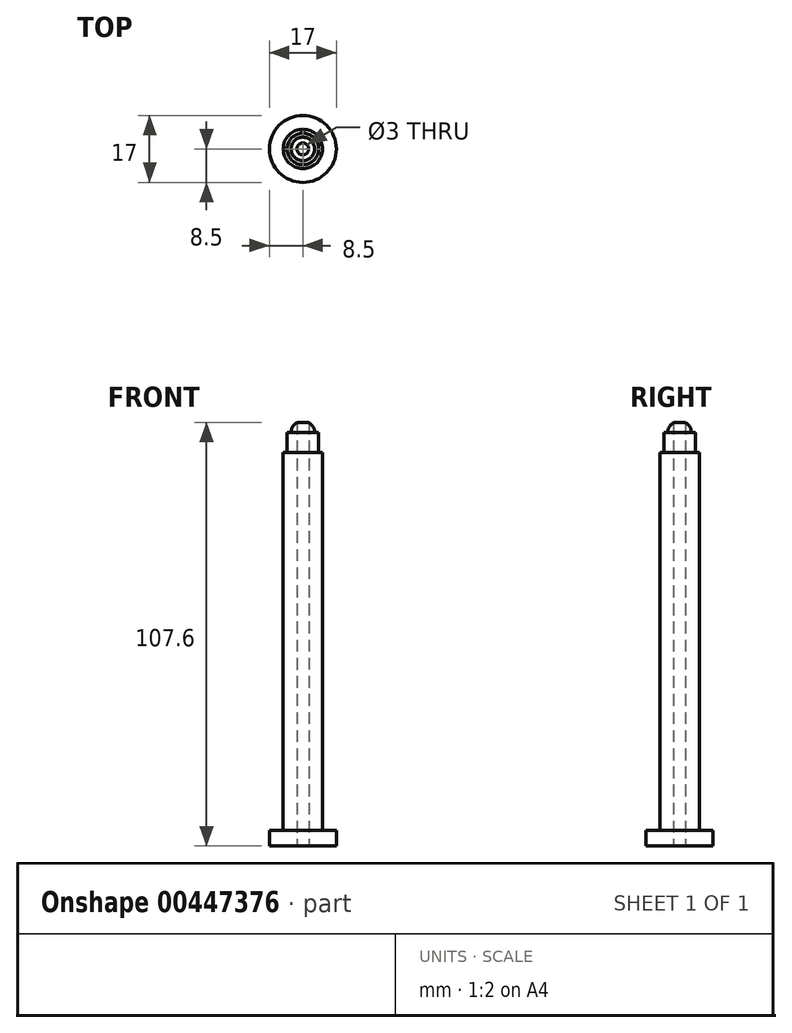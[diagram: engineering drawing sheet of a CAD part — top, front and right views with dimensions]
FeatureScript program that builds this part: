
annotation { "Feature Type Name" : "Feature", "Feature Type Description" : "" }
export const myFeature = defineFeature(function(context is Context, id is Id, definition is map)
    precondition{}
    {
        {
            var Q0;
            Q0=qCreatedBy(makeId("Top.planeOp"),FACE);
            var sketch = newSketch(context, id + "F0", { "sketchPlane" : qUnion([Q0])});
            skCircle(sketch, "E0", {"center": v(0, 0) * mm, "radius": 8.5 * mm});
            skSolve(sketch);
        }
        {
            var Q0;
            Q0=qSketchRegion(id+"F0",true);
            extrude(context, id + "F1", {"entities" : qUnion([Q0]), "depth" : 4 * mm});
        }
        {
            var Q0;
            Q0=qCreatedBy(makeId("Top.planeOp"),FACE);
            var sketch = newSketch(context, id + "F2", { "sketchPlane" : qUnion([Q0])});
            skCircle(sketch, "E1", {"center": v(0, 0) * mm, "radius": 5 * mm});
            skSolve(sketch);
        }
        {
            var Q0;
            Q0=qSketchRegion(id+"F2",true);
            extrude(context, id + "F3", {"entities" : qUnion([Q0]), "operationType" : NewBodyOperationType.ADD, "depth" : 100 * mm});
        }
        {
            var Q0;
            Q0=qCreatedBy(makeId("Right.planeOp"),FACE);
            var sketch = newSketch(context, id + "F4", { "sketchPlane" : qUnion([Q0])});
            skLineSegment(sketch, "E2", {"start": v(0, 105) * mm, "end": v(0, 100) * mm});
            skLineSegment(sketch, "E3", {"start": v(0, 100) * mm, "end": v(4, 100) * mm});
            skLineSegment(sketch, "E4", {"start": v(4, 100) * mm, "end": v(4, 105) * mm});
            skLineSegment(sketch, "E5", {"start": v(4, 105) * mm, "end": v(0, 105) * mm});
            skSolve(sketch);
        }
        {
            var Q0;
            Q0=makeQuery(id+"F4.imprint","IMPRINT",FACE,{"disambiguationData":[TD([[makeQuery(id+"F4.imprint","IMPRINT",EDGE,{"derivedFrom":sQuery(id+"F4.wireOp",EDGE,"E2")}),1.0]])]});
            var Q1;
            Q1=sQuery(id+"F4.wireOp",EDGE,"E2");
            revolve(context, id + "F5", {"operationType" : NewBodyOperationType.ADD, "entities" : qUnion([Q0]), "axis" : qUnion([Q1]), "revolveType" : RevolveType.FULL});
        }
        {
            var Q0;
            Q0=qCreatedBy(makeId("Right.planeOp"),FACE);
            var sketch = newSketch(context, id + "F6", { "sketchPlane" : qUnion([Q0])});
            skLineSegment(sketch, "E6", {"start": v(0, 108) * mm, "end": v(0, 105) * mm});
            skLineSegment(sketch, "E7", {"start": v(0, 105) * mm, "end": v(3, 105) * mm});
            skArc(sketch, "E8", {"start": v(3, 105) * mm, "mid": v(2.12, 107.12) * mm, "end": v(0, 108) * mm});
            skSolve(sketch);
        }
        {
            var Q0;
            Q0=makeQuery(id+"F6.imprint","IMPRINT",FACE,{"disambiguationData":[TD([[makeQuery(id+"F6.imprint","IMPRINT",EDGE,{"derivedFrom":sQuery(id+"F6.wireOp",EDGE,"E6")}),1.0]])]});
            var Q1;
            Q1=sQuery(id+"F6.wireOp",EDGE,"E6");
            revolve(context, id + "F7", {"operationType" : NewBodyOperationType.ADD, "entities" : qUnion([Q0]), "axis" : qUnion([Q1]), "revolveType" : RevolveType.FULL});
        }
        {
            var Q0;
            Q0=qCreatedBy(makeId("Top.planeOp"),FACE);
            var sketch = newSketch(context, id + "F8", { "sketchPlane" : qUnion([Q0])});
            skCircle(sketch, "E9", {"center": v(0, 0) * mm, "radius": 1.5 * mm});
            skSolve(sketch);
        }
        {
            var Q0;
            Q0 = qSketchRegion(id + "F8", true);
            extrude(context, id + "F9", {"entities" : qUnion([Q0]), "operationType" : NewBodyOperationType.REMOVE, "depth" : 109.1 * mm});
        }
    });
